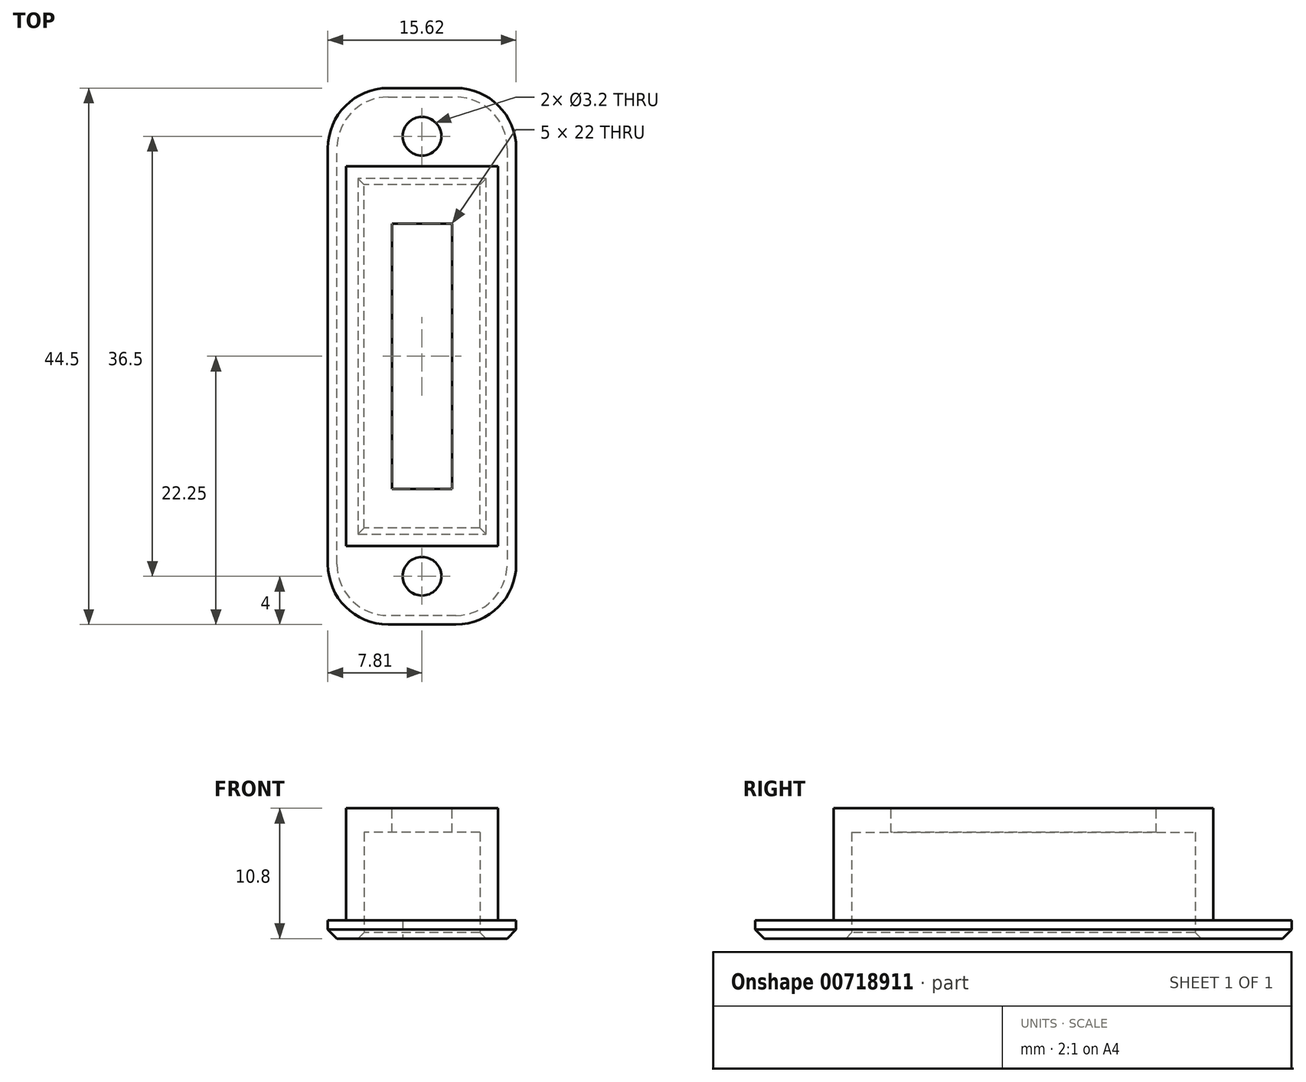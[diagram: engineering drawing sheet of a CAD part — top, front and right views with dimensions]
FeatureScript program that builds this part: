
annotation { "Feature Type Name" : "Feature", "Feature Type Description" : "" }
export const myFeature = defineFeature(function(context is Context, id is Id, definition is map)
    precondition{}
    {
        {
            var Q0;
            Q0=qCreatedBy(makeId("Top.planeOp"),FACE);
            var sketch = newSketch(context, id + "F0", { "sketchPlane" : qUnion([Q0])});
            skLineSegment(sketch, "E0.bottom", {"start": v(4.8, -14.25) * mm, "end": v(-4.81, -14.25) * mm});
            skLineSegment(sketch, "E0.top", {"start": v(4.8, 14.25) * mm, "end": v(-4.81, 14.25) * mm});
            skLineSegment(sketch, "E0.left", {"start": v(4.8, -14.25) * mm, "end": v(4.8, 14.25) * mm});
            skLineSegment(sketch, "E0.right", {"start": v(-4.81, -14.25) * mm, "end": v(-4.81, 14.25) * mm});
            skPoint(sketch, "E0.middle", {"position": v(0, 0) * mm});
            skLineSegment(sketch, "E1.bottom", {"start": v(-2.81, 22.25) * mm, "end": v(2.81, 22.25) * mm});
            skLineSegment(sketch, "E1.top", {"start": v(-2.81, -22.25) * mm, "end": v(2.81, -22.25) * mm});
            skLineSegment(sketch, "E1.left", {"start": v(-7.81, 17.25) * mm, "end": v(-7.81, -17.25) * mm});
            skLineSegment(sketch, "E1.right", {"start": v(7.81, 17.25) * mm, "end": v(7.81, -17.25) * mm});
            skPoint(sketch, "E2.visualSharp", {"position": v(-7.81, 22.25) * mm});
            skArc(sketch, "E2.filletArc", {"start": v(-2.81, 22.25) * mm, "mid": v(-6.35, 20.79) * mm, "end": v(-7.81, 17.25) * mm});
            skPoint(sketch, "E3.visualSharp", {"position": v(7.81, 22.25) * mm});
            skArc(sketch, "E3.filletArc", {"start": v(7.81, 17.25) * mm, "mid": v(6.35, 20.79) * mm, "end": v(2.81, 22.25) * mm});
            skPoint(sketch, "E4.visualSharp", {"position": v(7.81, -22.25) * mm});
            skArc(sketch, "E4.filletArc", {"start": v(2.81, -22.25) * mm, "mid": v(6.35, -20.79) * mm, "end": v(7.81, -17.25) * mm});
            skPoint(sketch, "E5.visualSharp", {"position": v(-7.81, -22.25) * mm});
            skArc(sketch, "E5.filletArc", {"start": v(-7.81, -17.25) * mm, "mid": v(-6.35, -20.79) * mm, "end": v(-2.81, -22.25) * mm});
            skSolve(sketch);
        }
        {
            var Q0;
            Q0 = qSketchRegion(id + "F0", true);
            extrude(context, id + "F1", {"entities" : qUnion([Q0]), "depth" : 1.5 * mm, "offsetDistance" : 25 * mm});
        }
        {
            var Q0;
            Q0=makeQuery(id+"F1.opExtrude","CAP_FACE",FACE,{"disambiguationData":[OSD([sQuery(id+"F0.wireOp",EDGE,"E0.bottom"),sQuery(id+"F0.wireOp",EDGE,"E0.top"),sQuery(id+"F0.wireOp",EDGE,"E0.left"),sQuery(id+"F0.wireOp",EDGE,"E0.right"),sQuery(id+"F0.wireOp",EDGE,"E1.bottom"),sQuery(id+"F0.wireOp",EDGE,"E1.top"),sQuery(id+"F0.wireOp",EDGE,"E1.left"),sQuery(id+"F0.wireOp",EDGE,"E1.right"),sQuery(id+"F0.wireOp",EDGE,"E2.filletArc"),sQuery(id+"F0.wireOp",EDGE,"E3.filletArc"),sQuery(id+"F0.wireOp",EDGE,"E4.filletArc"),sQuery(id+"F0.wireOp",EDGE,"E5.filletArc")])],"isStart":false});
            var sketch = newSketch(context, id + "F2", { "sketchPlane" : qUnion([Q0])});
            skLineSegment(sketch, "E6.0", {"start": v(4.8, 14.25) * mm, "end": v(-4.81, 14.25) * mm});
            skLineSegment(sketch, "E7.0", {"start": v(-4.81, -14.25) * mm, "end": v(-4.81, 14.25) * mm});
            skLineSegment(sketch, "E8.0", {"start": v(4.8, -14.25) * mm, "end": v(4.8, 14.25) * mm});
            skLineSegment(sketch, "E9.0", {"start": v(4.8, -14.25) * mm, "end": v(-4.81, -14.25) * mm});
            skLineSegment(sketch, "E10.0", {"start": v(6.3, 15.75) * mm, "end": v(-6.31, 15.75) * mm});
            skLineSegment(sketch, "E10.1", {"start": v(6.3, -15.75) * mm, "end": v(6.3, 15.75) * mm});
            skLineSegment(sketch, "E10.2", {"start": v(6.3, -15.75) * mm, "end": v(-6.31, -15.75) * mm});
            skLineSegment(sketch, "E10.3", {"start": v(-6.31, -15.75) * mm, "end": v(-6.31, 15.75) * mm});
            skSolve(sketch);
        }
        {
            var Q0;
            Q0 = qSketchRegion(id + "F2", true);
            extrude(context, id + "F3", {"entities" : qUnion([Q0]), "operationType" : NewBodyOperationType.ADD, "depth" : (8.8 - 1.5) * mm, "offsetDistance" : 25 * mm});
        }
        {
            var Q0;
            Q0=makeQuery(id+"F3.opExtrude","CAP_FACE",FACE,{"disambiguationData":[OSD([sQuery(id+"F2.wireOp",EDGE,"E6.0"),sQuery(id+"F2.wireOp",EDGE,"E7.0"),sQuery(id+"F2.wireOp",EDGE,"E8.0"),sQuery(id+"F2.wireOp",EDGE,"E9.0"),sQuery(id+"F2.wireOp",EDGE,"E10.0"),sQuery(id+"F2.wireOp",EDGE,"E10.1"),sQuery(id+"F2.wireOp",EDGE,"E10.2"),sQuery(id+"F2.wireOp",EDGE,"E10.3")])],"isStart":false});
            var sketch = newSketch(context, id + "F4", { "sketchPlane" : qUnion([Q0])});
            skLineSegment(sketch, "E11.0", {"start": v(-6.31, -15.75) * mm, "end": v(-6.31, 15.75) * mm});
            skLineSegment(sketch, "E12.0", {"start": v(6.3, -15.75) * mm, "end": v(-6.31, -15.75) * mm});
            skLineSegment(sketch, "E13.0", {"start": v(6.3, -15.75) * mm, "end": v(6.3, 15.75) * mm});
            skLineSegment(sketch, "E14.0", {"start": v(6.3, 15.75) * mm, "end": v(-6.31, 15.75) * mm});
            skSolve(sketch);
        }
        {
            var Q0;
            Q0 = qSketchRegion(id + "F4", true);
            extrude(context, id + "F5", {"entities" : qUnion([Q0]), "operationType" : NewBodyOperationType.ADD, "depth" : 2 * mm, "offsetDistance" : 25 * mm});
        }
        {
            var Q0;
            Q0=makeQuery(id+"F5.opExtrude","CAP_FACE",FACE,{"disambiguationData":[OSD([sQuery(id+"F4.wireOp",EDGE,"E11.0"),sQuery(id+"F4.wireOp",EDGE,"E12.0"),sQuery(id+"F4.wireOp",EDGE,"E13.0"),sQuery(id+"F4.wireOp",EDGE,"E14.0")])],"isStart":false});
            var sketch = newSketch(context, id + "F6", { "sketchPlane" : qUnion([Q0])});
            skLineSegment(sketch, "E15.bottom", {"start": v(2.5, 11) * mm, "end": v(-2.5, 11) * mm});
            skLineSegment(sketch, "E15.top", {"start": v(2.5, -11) * mm, "end": v(-2.5, -11) * mm});
            skLineSegment(sketch, "E15.left", {"start": v(2.5, 11) * mm, "end": v(2.5, -11) * mm});
            skLineSegment(sketch, "E15.right", {"start": v(-2.5, 11) * mm, "end": v(-2.5, -11) * mm});
            skPoint(sketch, "E15.middle", {"position": v(0, 0) * mm});
            skSolve(sketch);
        }
        {
            var Q0;
            Q0 = qSketchRegion(id + "F6", true);
            extrude(context, id + "F7", {"entities" : qUnion([Q0]), "operationType" : NewBodyOperationType.REMOVE, "oppositeDirection" : true, "depth" : 25 * mm, "offsetDistance" : 25 * mm});
        }
        {
            var Q0;
            Q0=makeQuery(id+"F1.opExtrude","CAP_FACE",FACE,{"disambiguationData":[OSD([sQuery(id+"F0.wireOp",EDGE,"E0.bottom"),sQuery(id+"F0.wireOp",EDGE,"E0.top"),sQuery(id+"F0.wireOp",EDGE,"E0.left"),sQuery(id+"F0.wireOp",EDGE,"E0.right"),sQuery(id+"F0.wireOp",EDGE,"E1.bottom"),sQuery(id+"F0.wireOp",EDGE,"E1.top"),sQuery(id+"F0.wireOp",EDGE,"E1.left"),sQuery(id+"F0.wireOp",EDGE,"E1.right"),sQuery(id+"F0.wireOp",EDGE,"E2.filletArc"),sQuery(id+"F0.wireOp",EDGE,"E3.filletArc"),sQuery(id+"F0.wireOp",EDGE,"E4.filletArc"),sQuery(id+"F0.wireOp",EDGE,"E5.filletArc")])],"isStart":true});
            var sketch = newSketch(context, id + "F8", { "sketchPlane" : qUnion([Q0])});
            skLineSegment(sketch, "E16", {"start": v(0, 22.25) * mm, "end": v(0, 14.25) * mm, "construction": true});
            skCircle(sketch, "E17", {"center": v(0, 18.25) * mm, "radius": 1.6 * mm});
            skCircle(sketch, "E18", {"center": v(0, 18.25) * mm, "radius": 3.38 * mm, "construction": true});
            skCircle(sketch, "E19.MirrorC", {"center": v(0, -18.25) * mm, "radius": 1.6 * mm});
            skSolve(sketch);
        }
        {
            var Q0;
            Q0 = qSketchRegion(id + "F8", true);
            extrude(context, id + "F9", {"entities" : qUnion([Q0]), "operationType" : NewBodyOperationType.REMOVE, "oppositeDirection" : true, "depth" : 25 * mm, "offsetDistance" : 25 * mm});
        }
        {
            var Q0;
            Q0=makeQuery(id+"F1.opExtrude","CAP_EDGE",EDGE,{"disambiguationData":[OSD([sQuery(id+"F0.wireOp",EDGE,"E1.right")])],"isStart":true});
            chamfer(context, id + "F10", {"entities" : qUnion([Q0]), "width" : .75 * mm, "tangentPropagation" : true});
        }
        {
            var Q0;
            Q0=makeQuery(id+"F1.opExtrude","CAP_EDGE",EDGE,{"disambiguationData":[OSD([sQuery(id+"F0.wireOp",EDGE,"E0.bottom")])],"isStart":true});
            var Q1;
            Q1=makeQuery(id+"F1.opExtrude","CAP_EDGE",EDGE,{"disambiguationData":[OSD([sQuery(id+"F0.wireOp",EDGE,"E0.left")])],"isStart":true});
            var Q2;
            Q2=makeQuery(id+"F1.opExtrude","CAP_EDGE",EDGE,{"disambiguationData":[OSD([sQuery(id+"F0.wireOp",EDGE,"E0.right")])],"isStart":true});
            var Q3;
            Q3=makeQuery(id+"F1.opExtrude","CAP_EDGE",EDGE,{"disambiguationData":[OSD([sQuery(id+"F0.wireOp",EDGE,"E0.top")])],"isStart":true});
            chamfer(context, id + "F11", {"entities" : qUnion([Q0, Q1, Q2, Q3]), "width" : .5 * mm, "tangentPropagation" : true});
        }
    });
